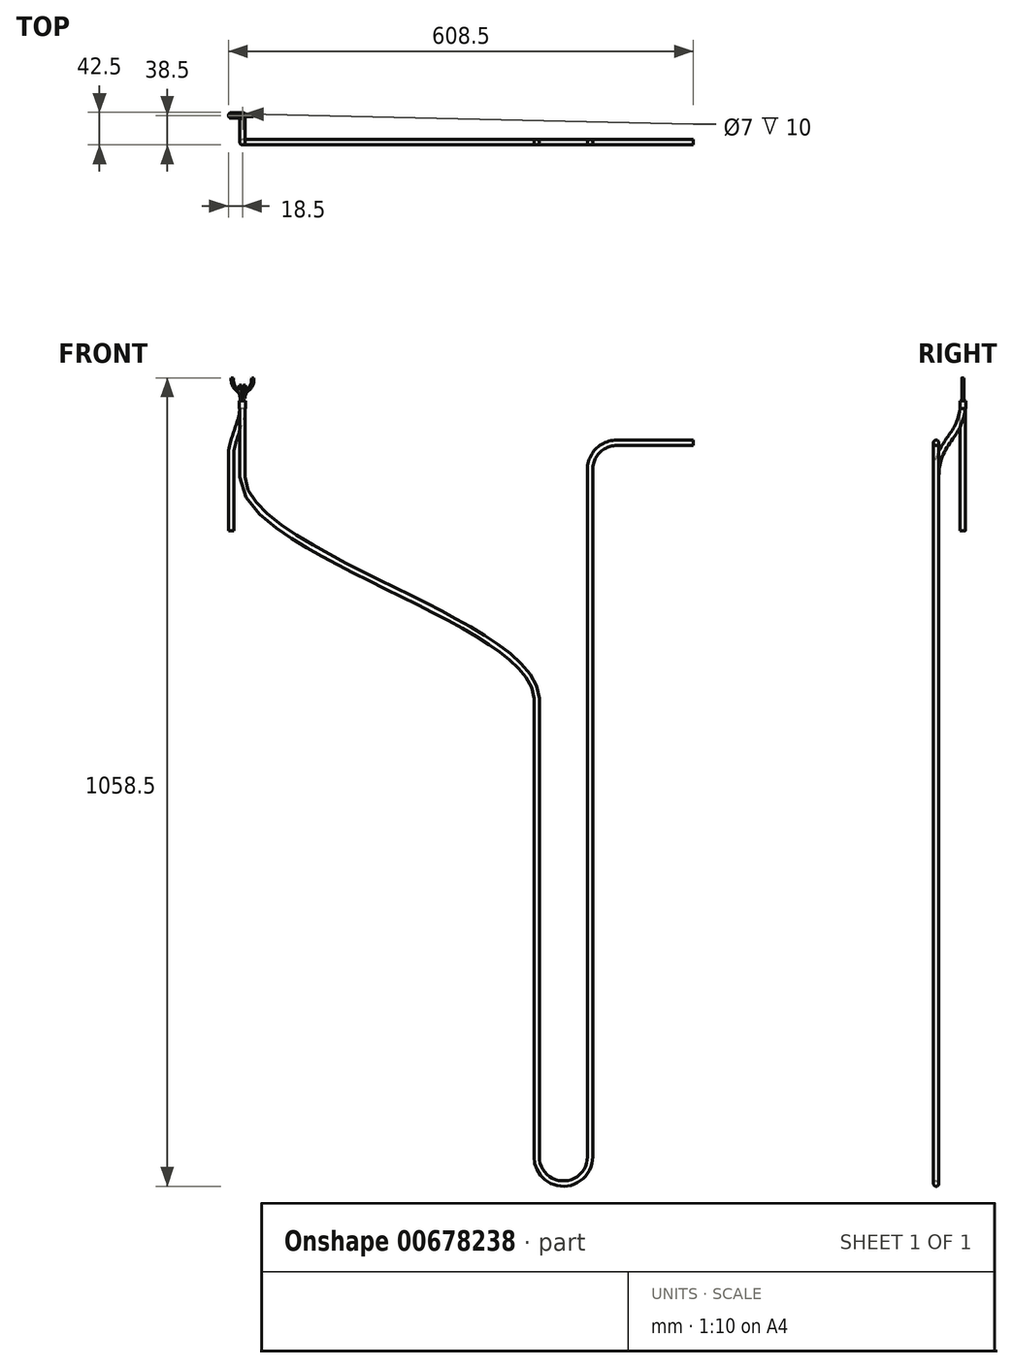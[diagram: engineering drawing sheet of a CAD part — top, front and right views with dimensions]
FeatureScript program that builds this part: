
annotation { "Feature Type Name" : "Feature", "Feature Type Description" : "" }
export const myFeature = defineFeature(function(context is Context, id is Id, definition is map)
    precondition{}
    {
        {
            var Q0;
            Q0=qCreatedBy(makeId("Top.planeOp"),FACE);
            var sketch = newSketch(context, id + "F0", { "sketchPlane" : qUnion([Q0])});
            skCircle(sketch, "E0", {"center": v(0, 0) * mm, "radius": 3.5 * mm});
            skSolve(sketch);
        }
        {
            var Q0;
            Q0=qCreatedBy(makeId("Front.planeOp"),FACE);
            var sketch = newSketch(context, id + "F1", { "sketchPlane" : qUnion([Q0])});
            skLineSegment(sketch, "E1", {"start": v(0, 0) * mm, "end": v(0, -10) * mm});
            skFitSpline(sketch, "E2", {"points": [v(0, -10) * mm, v(-15, -70) * mm], "startDerivative": vector(0, -45) * mm, "endDerivative": vector(0, -45) * mm});
            skLineSegment(sketch, "E3", {"start": v(-15, -70) * mm, "end": v(-15, -170) * mm});
            skSolve(sketch);
        }
        {
            var Q0;
            Q0=qSketchRegion(id+"F0",true);
            var Q1;
            Q1=qConstructionFilter(qBodyType(qCreatedBy(id+"F1",EDGE),BodyType.WIRE),ConstructionObject.NO);
            sweep(context, id + "F2", {"profiles" : qUnion([Q0]), "path" : qUnion([Q1])});
        }
        {
            var Q0;
            Q0=makeQuery(id+"F2.opSweep","CAP_FACE",FACE,{"disambiguationData":[OSD([sQuery(id+"F0.wireOp",EDGE,"E0"),sQuery(id+"F1.wireOp",VERTEX,"E1.start")])],"isStart":true});
            var sketch = newSketch(context, id + "F3", { "sketchPlane" : qUnion([Q0])});
            skCircle(sketch, "E4", {"center": v(1.5, 0) * mm, "radius": 1.5 * mm});
            skSolve(sketch);
        }
        {
            var Q0;
            Q0=qCreatedBy(makeId("Front.planeOp"),FACE);
            var sketch = newSketch(context, id + "F4", { "sketchPlane" : qUnion([Q0])});
            skFitSpline(sketch, "E5", {"points": [v(1.5, 0) * mm, v(2.5, 15) * mm], "startDerivative": vector(0, 15) * mm, "endDerivative": vector(0, 15) * mm});
            skLineSegment(sketch, "E6", {"start": v(2.5, 15) * mm, "end": v(2.5, 20) * mm});
            skSolve(sketch);
        }
        {
            var Q0;
            Q0=qSketchRegion(id+"F3",true);
            var Q1;
            Q1=qConstructionFilter(qBodyType(qCreatedBy(id+"F4",EDGE),BodyType.WIRE),ConstructionObject.NO);
            sweep(context, id + "F5", {"profiles" : qUnion([Q0]), "path" : qUnion([Q1])});
        }
        {
            var Q0;
            Q0=makeQuery(id+"F5.opSweep","SWEPT_BODY",BODY,{"disambiguationData":[OSD([sQuery(id+"F3.wireOp",EDGE,"E4"),sQuery(id+"F4.wireOp",EDGE,"E6")])]});
            var Q1;
            Q1=qCreatedBy(makeId("Right.planeOp"),FACE);
            mirror(context, id + "F6", {"entities" : qUnion([Q0]), "mirrorPlane" : qUnion([Q1])});
        }
        {
            var Q0;
            Q0=makeQuery(id+"F2.opSweep","CAP_FACE",FACE,{"disambiguationData":[OSD([sQuery(id+"F0.wireOp",EDGE,"E0"),sQuery(id+"F1.wireOp",VERTEX,"E1.start")])],"isStart":true});
            var sketch = newSketch(context, id + "F7", { "sketchPlane" : qUnion([Q0])});
            skCircle(sketch, "E7.0", {"center": v(0, 0) * mm, "radius": 3.5 * mm});
            skCircle(sketch, "E8.0", {"center": v(0, 0) * mm, "radius": 4 * mm});
            skSolve(sketch);
        }
        {
            var Q0;
            Q0=qSketchRegion(id+"F7",true);
            extrude(context, id + "F8", {"entities" : qUnion([Q0]), "oppositeDirection" : true, "depth" : 10 * mm, "offsetDistance" : 25 * mm});
        }
        {
            var Q0;
            Q0=qCreatedBy(makeId("Front.planeOp"),FACE);
            var sketch = newSketch(context, id + "F9", { "sketchPlane" : qUnion([Q0])});
            skFitSpline(sketch, "E9", {"points": [v(13.5, 30) * mm, v(7.5, 15) * mm, v(1.5, 0) * mm], "startDerivative": vector(0, -60) * mm, "endDerivative": vector(0, -60) * mm});
            skLineSegment(sketch, "E10", {"start": v(13.5, 20) * mm, "end": v(13.5, 30) * mm, "construction": true});
            skLineSegment(sketch, "E11", {"start": v(1.5, 0) * mm, "end": v(13.5, 30) * mm, "construction": true});
            skLineSegment(sketch, "E12", {"start": v(1.5, 10) * mm, "end": v(1.5, 0) * mm, "construction": true});
            skSolve(sketch);
        }
        {
            var Q0;
            Q0=qSketchRegion(id+"F3",true);
            var Q1;
            Q1=sQuery(id+"F9.wireOp",EDGE,"E9");
            sweep(context, id + "F10", {"profiles" : qUnion([Q0]), "path" : qUnion([Q1])});
        }
        {
            var Q0;
            Q0=makeQuery(id+"F10.opSweep","SWEPT_BODY",BODY,{"disambiguationData":[OSD([sQuery(id+"F3.wireOp",EDGE,"E4"),sQuery(id+"F9.wireOp",EDGE,"E9")])]});
            var Q1;
            Q1=qCreatedBy(makeId("Right.planeOp"),FACE);
            mirror(context, id + "F11", {"entities" : qUnion([Q0]), "mirrorPlane" : qUnion([Q1])});
        }
        {
            var Q0;
            Q0=qCreatedBy(makeId("Right.planeOp"),FACE);
            var sketch = newSketch(context, id + "F12", { "sketchPlane" : qUnion([Q0])});
            skFitSpline(sketch, "E13", {"points": [v(0, 0) * mm, v(-17.5, -50) * mm, v(-35, -100) * mm], "startDerivative": vector(0, -150) * mm, "endDerivative": vector(0, -150) * mm});
            skLineSegment(sketch, "E14", {"start": v(0, -25) * mm, "end": v(0, 0) * mm, "construction": true});
            skLineSegment(sketch, "E15", {"start": v(-35, -75) * mm, "end": v(-35, -100) * mm, "construction": true});
            skLineSegment(sketch, "E16", {"start": v(-35, -100) * mm, "end": v(0, 0) * mm, "construction": true});
            skSolve(sketch);
        }
        {
            var Q0;
            Q0=qCreatedBy(makeId("Front.planeOp"),FACE);
            var Q1;
            Q1=sQuery(id+"F12.wireOp",VERTEX,"E16.start");
            cPlane(context, id + "F13", {"entities" : qUnion([Q0, Q1]), "cplaneType" : CPlaneType.PLANE_POINT, "offset" : 25 * mm, "width" : 150 * mm, "height" : 150 * mm});
        }
        {
            var Q0;
            Q0=qCreatedBy(id+"F13.planeOp",FACE);
            var sketch = newSketch(context, id + "F14", { "sketchPlane" : qUnion([Q0])});
            skLineSegment(sketch, "E17", {"start": v(385, -390) * mm, "end": v(385, -990) * mm});
            skLineSegment(sketch, "E18", {"start": v(455, -990) * mm, "end": v(455, -90) * mm});
            skArc(sketch, "E19", {"start": v(385, -990) * mm, "mid": v(420, -1025) * mm, "end": v(455, -990) * mm});
            skArc(sketch, "E20", {"start": v(490, -55) * mm, "mid": v(465.25, -65.25) * mm, "end": v(455, -90) * mm});
            skLineSegment(sketch, "E21", {"start": v(490, -55) * mm, "end": v(590, -55) * mm});
            skFitSpline(sketch, "E22", {"points": [v(385, -390) * mm, v(192.5, -245) * mm, v(0, -100) * mm], "startDerivative": vector(0, 300) * mm, "endDerivative": vector(0, 300) * mm});
            skLineSegment(sketch, "E23", {"start": v(0, -150) * mm, "end": v(0, -100) * mm, "construction": true});
            skLineSegment(sketch, "E24", {"start": v(385, -340) * mm, "end": v(385, -390) * mm, "construction": true});
            skLineSegment(sketch, "E25", {"start": v(385, -390) * mm, "end": v(0, -100) * mm, "construction": true});
            skSolve(sketch);
        }
        {
            var Q0;
            Q0=qSketchRegion(id+"F0",true);
            var Q1;
            Q1=qConstructionFilter(qBodyType(qCreatedBy(id+"F12",EDGE),BodyType.WIRE),ConstructionObject.NO);
            var Q2;
            Q2=qConstructionFilter(qBodyType(qCreatedBy(id+"F14",EDGE),BodyType.WIRE),ConstructionObject.NO);
            sweep(context, id + "F15", {"profiles" : qUnion([Q0]), "path" : qUnion([Q1, Q2])});
        }
    });
